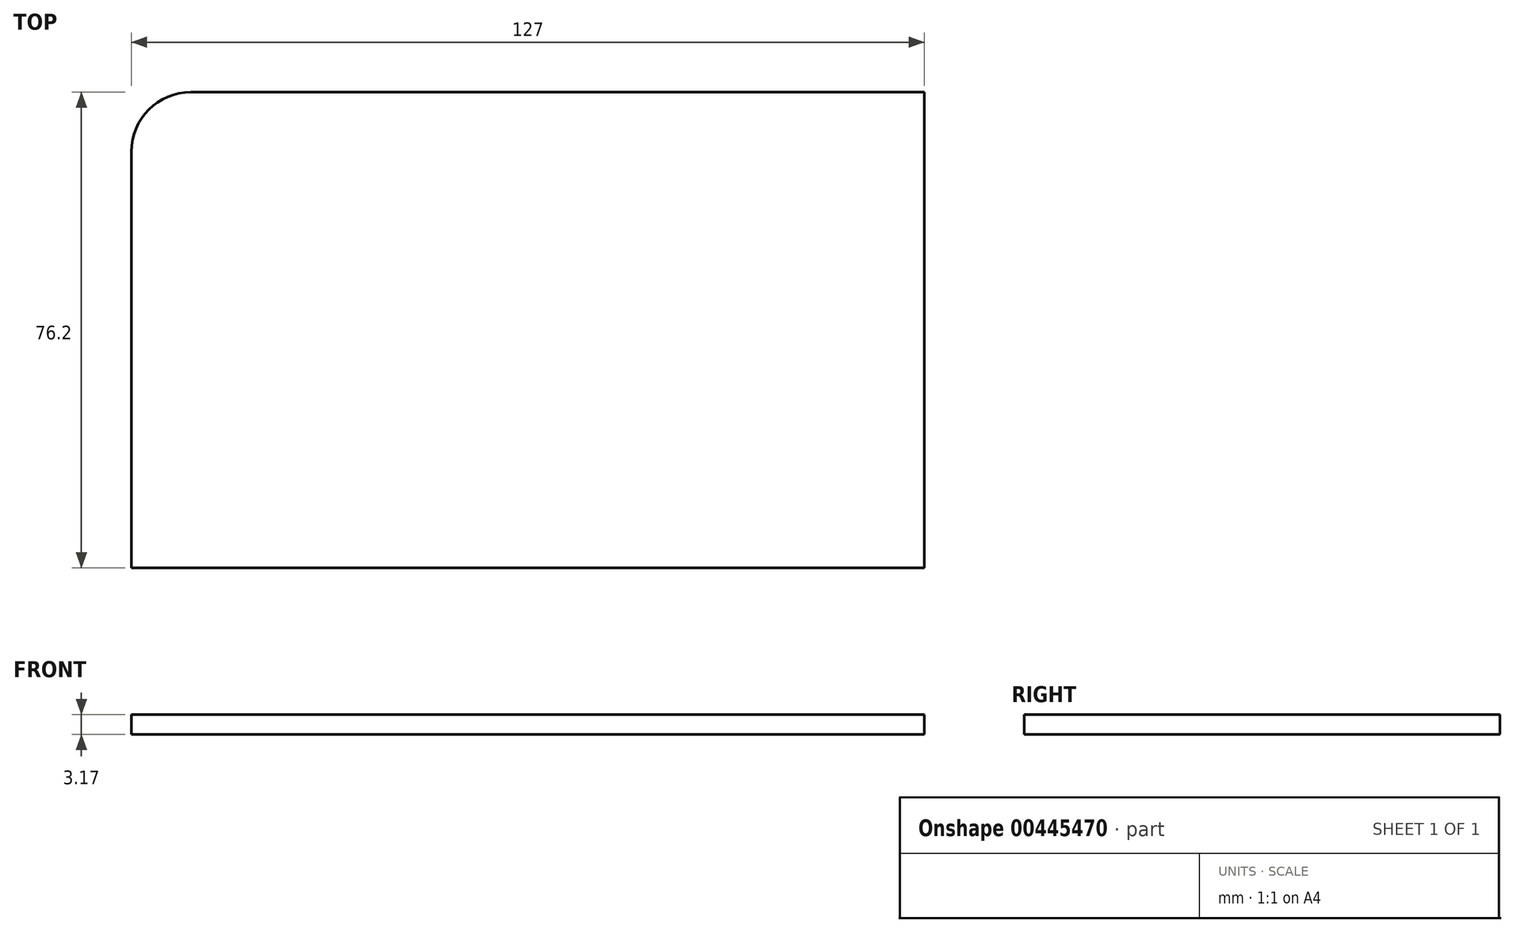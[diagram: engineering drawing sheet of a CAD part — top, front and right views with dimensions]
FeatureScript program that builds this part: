
annotation { "Feature Type Name" : "Feature", "Feature Type Description" : "" }
export const myFeature = defineFeature(function(context is Context, id is Id, definition is map)
    precondition{}
    {
        {
            var Q0;
            Q0=qCreatedBy(makeId("Top.planeOp"),FACE);
            var sketch = newSketch(context, id + "F0", { "sketchPlane" : qUnion([Q0])});
            skLineSegment(sketch, "E0.bottom", {"start": v(-53.96, 38.1) * mm, "end": v(63.5, 38.1) * mm});
            skLineSegment(sketch, "E0.top", {"start": v(-63.5, -38.1) * mm, "end": v(63.5, -38.1) * mm});
            skLineSegment(sketch, "E0.left", {"start": v(-63.5, 28.56) * mm, "end": v(-63.5, -38.1) * mm});
            skLineSegment(sketch, "E0.right", {"start": v(63.5, 38.1) * mm, "end": v(63.5, -38.1) * mm});
            skPoint(sketch, "E0.middle", {"position": v(0, 0) * mm});
            skPoint(sketch, "E1.visualSharp", {"position": v(-63.5, 38.1) * mm});
            skArc(sketch, "E1.filletArc", {"start": v(-53.96, 38.1) * mm, "mid": v(-60.7, 35.3) * mm, "end": v(-63.5, 28.56) * mm});
            skSolve(sketch);
        }
        {
            var Q0;
            Q0 = qSketchRegion(id + "F0", true);
            extrude(context, id + "F1", {"entities" : qUnion([Q0]), "depth" : 3.17 * mm});
        }
    });
